# Revit family: Lighting_Emergency&Security_Linergy_Cristal-wall
name_source: partatom
category: Lighting Fixtures
revit_build: Autodesk Revit 2018 (Build: 20190510_1515(x64)
units: mm (PartAtom-declared; Revit-internal decimal feet)

## family parameters
Cut with Voids When Loaded = No
Host = Face
Light Source = Yes
OmniClass Number = 23.35.47.13
OmniClass Title = Emergency Lighting
Part Type = Normal
Room Calculation Point = No
Round Connector Dimension = Use Diameter
Shared = No

## types (1)
- Default - please load Revit Family Type Catalog
    Apparent Load = 0 VA
    Apparent Load Phase 2 = 0 VA
    Apparent Load Phase 3 = 0 VA
    BIMobject category = Emergency & Security
    Battery = 0
    Color Filter = 16777215
    Cover material = Linergy - Plastic - Polycarbonate Transparent high polished
    Default Elevation = 1219 mm
    Description = LED Emergency lighting luminaire. Designed exclusively for wall mount.
    Design country = Italy
    Dimming Lamp Color Temperature Shift = <None>
    Duration = 0 h
    Edition number = 1
    Flux M = 935 lm
    Flux N/M = 0 lm
    Function = Spy Center 24
    IFC Classification = Light Fixture
    Input power = 14 VA
    Installation instructions = https://www.linergy.it
    Insulation class = III
    Lamp type = L
    Main material = Linergy - Plastic - Polycarbonate Light Grey RAL 7035 polished
    Manufacturer = Linergy
    Manufacturer country = Italy
    Manufacturer name = Linergy
    Material main = PC/ABS
    Material secondary = Electronic & optical components
    Model = CW2105
    Number of Poles = 1
    OmniClass Code = 23-35 47 13
    OmniClass Description = Emergency Lighting
    Photometric Web File = generic
    Power supply = 230 Vac
    Product Guid = 899327b0-aca3-4f1b-8766-ba1273370e66
    Product SKU = cristal-wall
    Product certification = https://www.linergy.it
    Product data url = https://bimobject.com
    Product family = Emergency luminaires
    Product group = Emergency luminaires
    Product name = CRISTAL WALL - Emergency lighting luminaire
    Product url = https://www.linergy.it
    Protection degree = IP65
    QR code = https://bimobject.com
    Secondary material = Linergy - Plastic - Polycarbonate Light grey metallizztion
    Technical description = https://www.linergy.it
    Tilt Angle = -90.00°
    URL = https://www.linergy.it
    URL - Article page = https://www.linergy.it
    URL - Photometric file (ldt) = https://www.linergy.it
    Voltage = 230 V

## geometry (parser evidence)
native form markers: Sweep x3
no freeform markers — native parametric forms only
